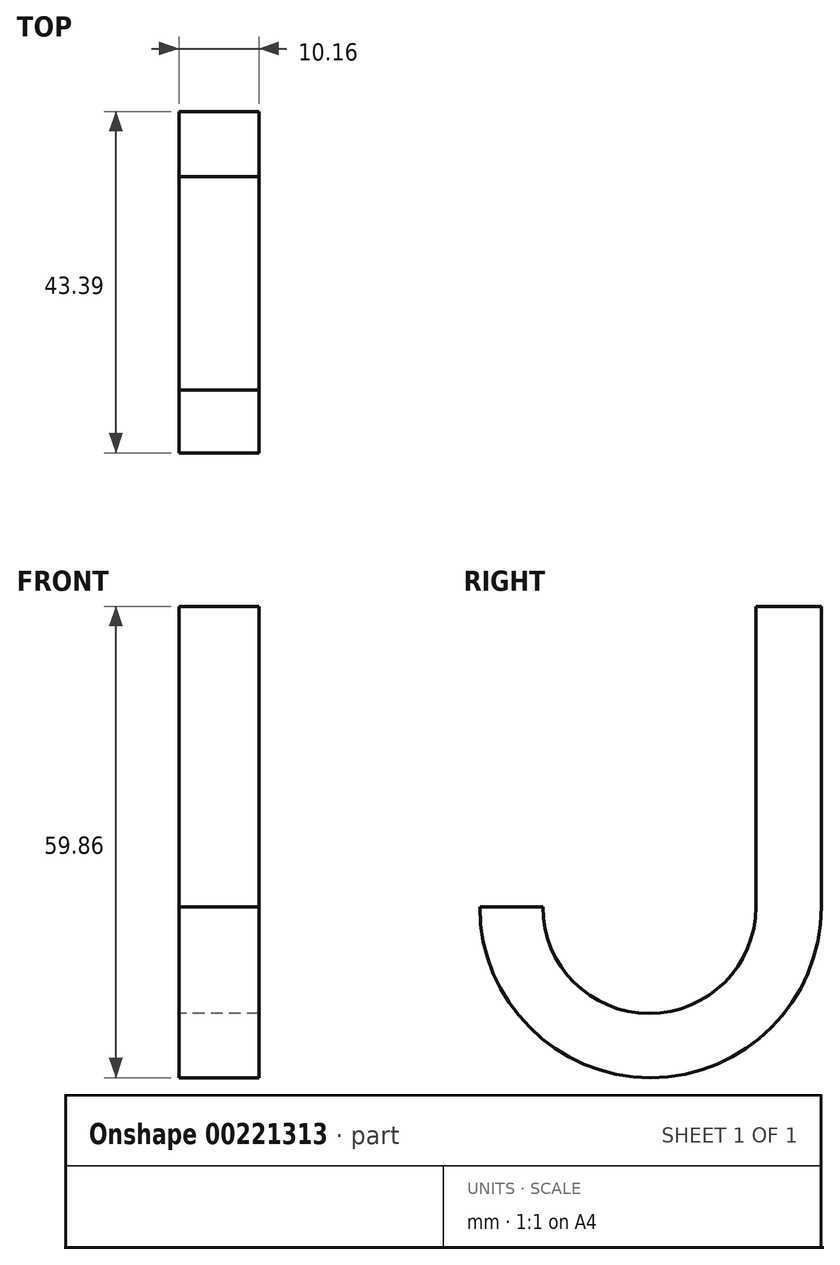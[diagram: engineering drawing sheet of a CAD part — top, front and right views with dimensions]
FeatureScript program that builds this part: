
annotation { "Feature Type Name" : "Feature", "Feature Type Description" : "" }
export const myFeature = defineFeature(function(context is Context, id is Id, definition is map)
    precondition{}
    {
        {
            var Q0;
            Q0=qCreatedBy(makeId("Right.planeOp"),FACE);
            var sketch = newSketch(context, id + "F0", { "sketchPlane" : qUnion([Q0])});
            skLineSegment(sketch, "E0.bottom", {"start": v(0, 34.47) * mm, "end": v(-8.3, 34.47) * mm});
            skLineSegment(sketch, "E0.left", {"start": v(0, 34.47) * mm, "end": v(0, -3.7) * mm});
            skLineSegment(sketch, "E0.right", {"start": v(-8.3, 34.47) * mm, "end": v(-8.3, -3.7) * mm});
            skArc(sketch, "E1", {"start": v(-35.39, -3.7) * mm, "mid": v(-21.85, -17.23) * mm, "end": v(-8.3, -3.7) * mm});
            skLineSegment(sketch, "E2", {"start": v(-35.39, -3.7) * mm, "end": v(-43.4, -3.7) * mm});
            skArc(sketch, "E3", {"start": v(-43.4, -3.7) * mm, "mid": v(-21.7, -25.39) * mm, "end": v(0, -3.7) * mm});
            skSolve(sketch);
        }
        {
            var Q0;
            Q0=makeQuery(id+"F0.imprint","IMPRINT",FACE,{"disambiguationData":[TD([[makeQuery(id+"F0.imprint","IMPRINT",EDGE,{"derivedFrom":sQuery(id+"F0.wireOp",EDGE,"E0.bottom")}),1.0]])]});
            extrude(context, id + "F1", {"entities" : qUnion([Q0]), "depth" : 10.16 * mm});
        }
    });
